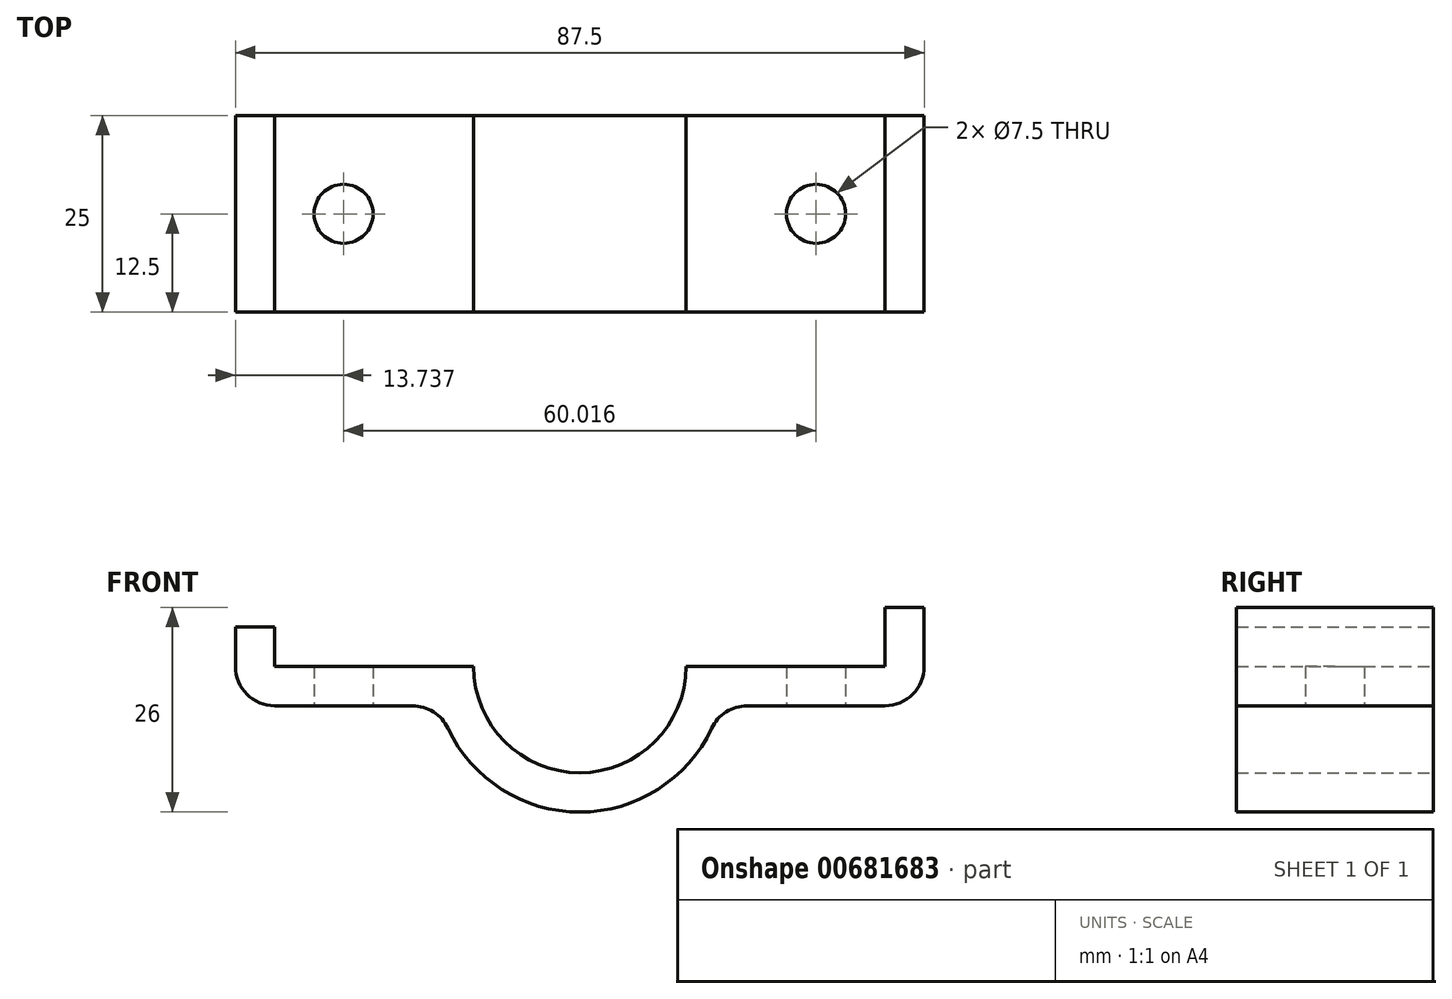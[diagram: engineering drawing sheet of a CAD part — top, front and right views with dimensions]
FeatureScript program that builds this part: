
annotation { "Feature Type Name" : "Feature", "Feature Type Description" : "" }
export const myFeature = defineFeature(function(context is Context, id is Id, definition is map)
    precondition{}
    {
        {
            var Q0;
            Q0=qCreatedBy(makeId("Front.planeOp"),FACE);
            var sketch = newSketch(context, id + "F0", { "sketchPlane" : qUnion([Q0])});
            skLineSegment(sketch, "E0", {"start": v(-54.94, 46.37) * mm, "end": v(-49.94, 46.37) * mm});
            skLineSegment(sketch, "E1", {"start": v(-49.94, 41.37) * mm, "end": v(-24.7, 41.37) * mm});
            skLineSegment(sketch, "E2", {"start": v(27.56, 41.37) * mm, "end": v(27.56, 48.87) * mm});
            skLineSegment(sketch, "E3", {"start": v(27.56, 48.87) * mm, "end": v(32.56, 48.87) * mm});
            skLineSegment(sketch, "E4", {"start": v(32.56, 48.87) * mm, "end": v(32.56, 41.37) * mm});
            skLineSegment(sketch, "E5", {"start": v(27.56, 36.37) * mm, "end": v(10.07, 36.37) * mm});
            skLineSegment(sketch, "E6", {"start": v(-54.94, 41.37) * mm, "end": v(-54.94, 46.37) * mm});
            skLineSegment(sketch, "E7", {"start": v(-49.94, 46.37) * mm, "end": v(-49.94, 41.37) * mm});
            skPoint(sketch, "E8", {"position": v(-11.2, 41.37) * mm});
            skPoint(sketch, "E9", {"position": v(-41.2, 41.37) * mm});
            skPoint(sketch, "E10", {"position": v(18.8, 41.37) * mm});
            skArc(sketch, "E11", {"start": v(-24.7, 41.37) * mm, "mid": v(-11.2, 27.87) * mm, "end": v(2.3, 41.37) * mm});
            skArc(sketch, "E12", {"start": v(-27.94, 33.5) * mm, "mid": v(-11.2, 22.87) * mm, "end": v(5.55, 33.5) * mm});
            skLineSegment(sketch, "E13.trimOffspring", {"start": v(-32.46, 36.37) * mm, "end": v(-49.94, 36.37) * mm});
            skLineSegment(sketch, "E14.trimOffspring", {"start": v(2.3, 41.37) * mm, "end": v(27.56, 41.37) * mm});
            skArc(sketch, "E15.filletArc", {"start": v(10.07, 36.37) * mm, "mid": v(7.4, 35.6) * mm, "end": v(5.55, 33.5) * mm});
            skPoint(sketch, "E16.visualSharp", {"position": v(32.56, 36.37) * mm});
            skArc(sketch, "E16.filletArc", {"start": v(27.56, 36.37) * mm, "mid": v(31.1, 37.84) * mm, "end": v(32.56, 41.37) * mm});
            skArc(sketch, "E17.filletArc", {"start": v(-27.94, 33.5) * mm, "mid": v(-29.78, 35.6) * mm, "end": v(-32.46, 36.37) * mm});
            skPoint(sketch, "E18.visualSharp", {"position": v(-54.94, 36.37) * mm});
            skArc(sketch, "E18.filletArc", {"start": v(-54.94, 41.37) * mm, "mid": v(-53.48, 37.84) * mm, "end": v(-49.94, 36.37) * mm});
            skSolve(sketch);
        }
        {
            var Q0;
            Q0 = qSketchRegion(id + "F0", true);
            extrude(context, id + "F1", {"entities" : qUnion([Q0]), "depth" : 25 * mm, "offsetDistance" : 25 * mm});
        }
        {
            var Q0;
            Q0=makeQuery(id+"F1.opExtrude","SWEPT_FACE",FACE,{"disambiguationData":[OSD([sQuery(id+"F0.wireOp",EDGE,"E13.trimOffspring")])]});
            var sketch = newSketch(context, id + "F2", { "sketchPlane" : qUnion([Q0])});
            skLineSegment(sketch, "E19.0.0", {"start": v(10.07, 0) * mm, "end": v(27.56, 0) * mm});
            skLineSegment(sketch, "E19.0.1", {"start": v(27.56, 0) * mm, "end": v(27.56, 25) * mm});
            skLineSegment(sketch, "E19.0.2", {"start": v(27.56, 25) * mm, "end": v(10.07, 25) * mm});
            skLineSegment(sketch, "E19.0.3", {"start": v(10.07, 25) * mm, "end": v(10.07, 0) * mm});
            skLineSegment(sketch, "E20.0.0", {"start": v(10.07, 25) * mm, "end": v(27.56, 25) * mm});
            skLineSegment(sketch, "E20.0.1", {"start": v(27.56, 25) * mm, "end": v(32.56, 25) * mm});
            skLineSegment(sketch, "E20.0.5", {"start": v(27.56, 25) * mm, "end": v(5.55, 25) * mm});
            skLineSegment(sketch, "E20.0.7", {"start": v(-27.94, 25) * mm, "end": v(-32.46, 25) * mm});
            skLineSegment(sketch, "E20.0.13", {"start": v(-32.46, 25) * mm, "end": v(-27.94, 25) * mm});
            skLineSegment(sketch, "E20.0.15", {"start": v(5.55, 25) * mm, "end": v(10.07, 25) * mm});
            skPoint(sketch, "E21", {"position": v(-41.2, 12.5) * mm});
            skPoint(sketch, "E22", {"position": v(18.81, 12.5) * mm});
            skPoint(sketch, "E20.0.3.end.orphan", {"position": v(27.56, 25) * mm});
            skPoint(sketch, "E20.0.3.start.orphan", {"position": v(32.56, 25) * mm});
            skPoint(sketch, "E20.0.11.end.orphan", {"position": v(-49.94, 25) * mm});
            skPoint(sketch, "E20.0.11.start.orphan", {"position": v(-54.94, 25) * mm});
            skPoint(sketch, "E20.0.9.end.orphan", {"position": v(-54.94, 25) * mm});
            skPoint(sketch, "E20.0.9.start.orphan", {"position": v(-49.94, 25) * mm});
            skPoint(sketch, "E23.orphan", {"position": v(2.3, 25) * mm});
            skPoint(sketch, "E24.orphan", {"position": v(-24.7, 25) * mm});
            skSolve(sketch);
        }
        {
            var Q0;
            Q0=sQuery(id+"F2.wireOp",VERTEX,"E21");
            var Q1;
            Q1=makeQuery(id+"F1.opExtrude","SWEPT_BODY",BODY,{"disambiguationData":[OSD([sQuery(id+"F0.wireOp",EDGE,"E0"),sQuery(id+"F0.wireOp",EDGE,"E1"),sQuery(id+"F0.wireOp",EDGE,"E2"),sQuery(id+"F0.wireOp",EDGE,"E3"),sQuery(id+"F0.wireOp",EDGE,"E4"),sQuery(id+"F0.wireOp",EDGE,"E5"),sQuery(id+"F0.wireOp",EDGE,"E6"),sQuery(id+"F0.wireOp",EDGE,"E7"),sQuery(id+"F0.wireOp",EDGE,"E11"),sQuery(id+"F0.wireOp",EDGE,"E12"),sQuery(id+"F0.wireOp",EDGE,"E13.trimOffspring"),sQuery(id+"F0.wireOp",EDGE,"E14.trimOffspring"),sQuery(id+"F0.wireOp",EDGE,"E15.filletArc"),sQuery(id+"F0.wireOp",EDGE,"E16.filletArc"),sQuery(id+"F0.wireOp",EDGE,"E17.filletArc"),sQuery(id+"F0.wireOp",EDGE,"E18.filletArc")])]});
            hole(context, id + "F3", {"style" : HoleStyle.SIMPLE, "endStyle" : HoleEndStyle.THROUGH, "holeDiameter" : 7.5 * mm, "majorDiameter" : 5 * mm, "isTappedThrough" : true, "tappedDepth" : 12 * mm, "tapClearance" : 3, "locations" : qUnion([Q0]), "scope" : qUnion([Q1])});
        }
        {
            var Q0;
            Q0=sQuery(id+"F2.wireOp",VERTEX,"E22");
            var Q1;
            Q1=makeQuery(id+"F1.opExtrude","SWEPT_BODY",BODY,{"disambiguationData":[OSD([sQuery(id+"F0.wireOp",EDGE,"E0"),sQuery(id+"F0.wireOp",EDGE,"E1"),sQuery(id+"F0.wireOp",EDGE,"E2"),sQuery(id+"F0.wireOp",EDGE,"E3"),sQuery(id+"F0.wireOp",EDGE,"E4"),sQuery(id+"F0.wireOp",EDGE,"E5"),sQuery(id+"F0.wireOp",EDGE,"E6"),sQuery(id+"F0.wireOp",EDGE,"E7"),sQuery(id+"F0.wireOp",EDGE,"E11"),sQuery(id+"F0.wireOp",EDGE,"E12"),sQuery(id+"F0.wireOp",EDGE,"E13.trimOffspring"),sQuery(id+"F0.wireOp",EDGE,"E14.trimOffspring"),sQuery(id+"F0.wireOp",EDGE,"E15.filletArc"),sQuery(id+"F0.wireOp",EDGE,"E16.filletArc"),sQuery(id+"F0.wireOp",EDGE,"E17.filletArc"),sQuery(id+"F0.wireOp",EDGE,"E18.filletArc")])]});
            hole(context, id + "F4", {"style" : HoleStyle.SIMPLE, "endStyle" : HoleEndStyle.THROUGH, "holeDiameter" : 7.5 * mm, "majorDiameter" : 5 * mm, "isTappedThrough" : true, "tappedDepth" : 12 * mm, "tapClearance" : 3, "locations" : qUnion([Q0]), "scope" : qUnion([Q1])});
        }
    });
